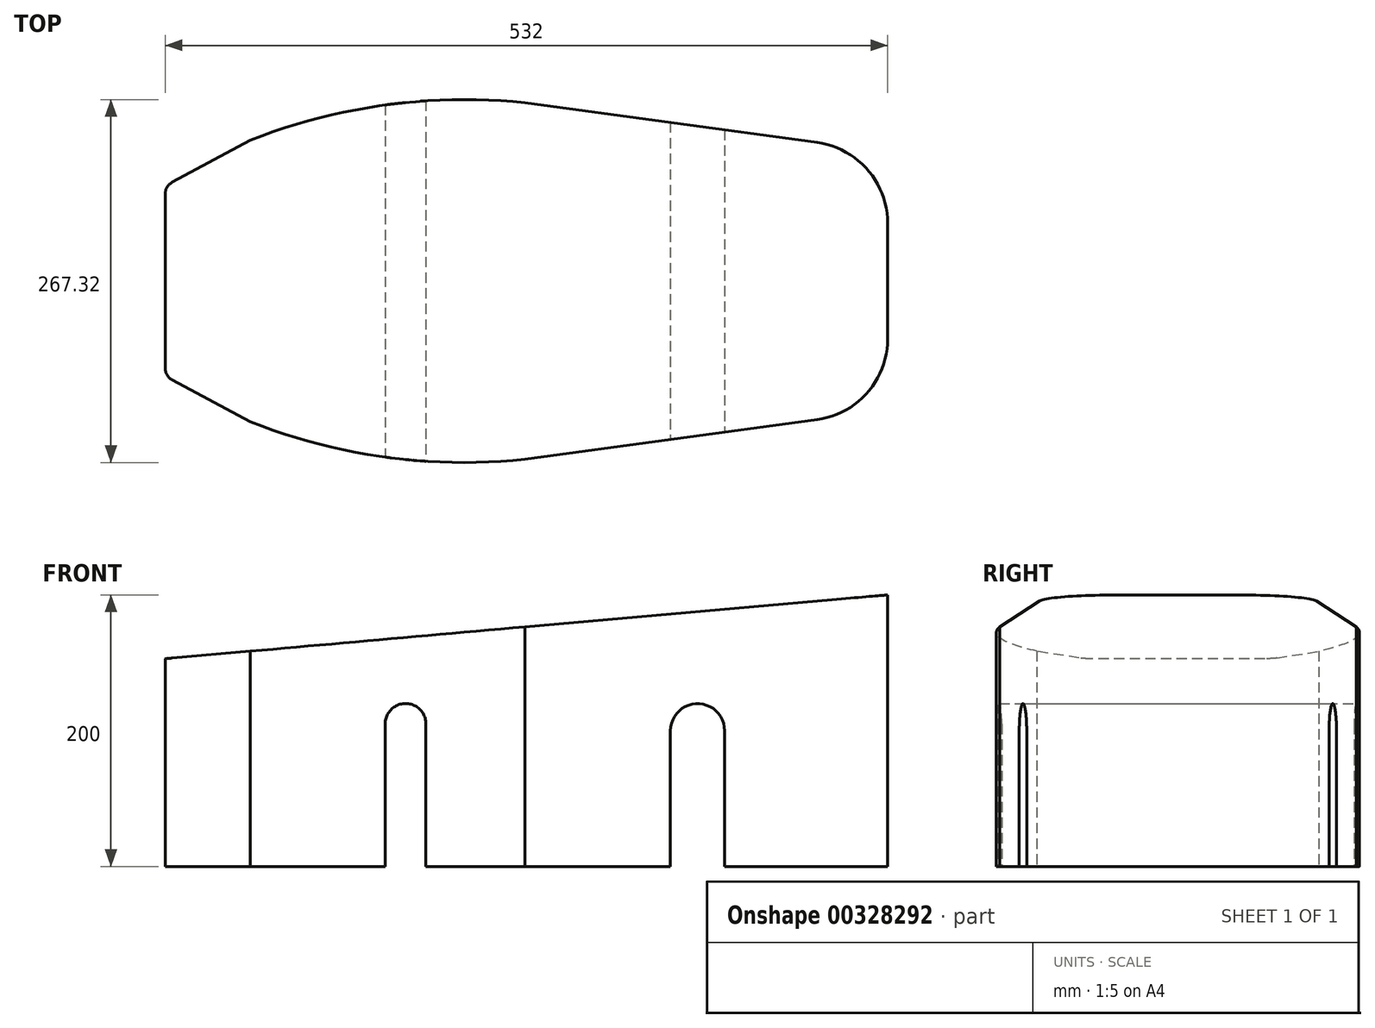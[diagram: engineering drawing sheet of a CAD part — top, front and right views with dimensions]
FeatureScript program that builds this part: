
annotation { "Feature Type Name" : "Feature", "Feature Type Description" : "" }
export const myFeature = defineFeature(function(context is Context, id is Id, definition is map)
    precondition{}
    {
        {
            var Q0;
            Q0=qCreatedBy(makeId("Top.planeOp"),FACE);
            var sketch = newSketch(context, id + "F0", { "sketchPlane" : qUnion([Q0])});
            skArc(sketch, "E0", {"start": v(-260.74, 72.83) * mm, "mid": v(-264.59, 69.15) * mm, "end": v(-266, 64.03) * mm});
            skLineSegment(sketch, "E1", {"start": v(-260.74, 72.83) * mm, "end": v(-203.32, 103.75) * mm});
            skArc(sketch, "E2", {"start": v(266, 42.61) * mm, "mid": v(251.2, 82.07) * mm, "end": v(214.1, 102.06) * mm});
            skLineSegment(sketch, "E3", {"start": v(-266, -64.03) * mm, "end": v(-266, 64.03) * mm});
            skLineSegment(sketch, "E4", {"start": v(-260.74, -72.83) * mm, "end": v(-203.32, -103.75) * mm});
            skArc(sketch, "E5", {"start": v(-266, -64.03) * mm, "mid": v(-264.59, -69.15) * mm, "end": v(-260.74, -72.83) * mm});
            skLineSegment(sketch, "E6", {"start": v(266, -42.61) * mm, "end": v(266, 42.61) * mm});
            skLineSegment(sketch, "E7", {"start": v(214.1, 102.06) * mm, "end": v(-1.08, 131.35) * mm});
            skArc(sketch, "E8", {"start": v(-1.08, 131.35) * mm, "mid": v(-103.86, 129.7) * mm, "end": v(-203.32, 103.75) * mm});
            skArc(sketch, "E9", {"start": v(214.1, -102.06) * mm, "mid": v(251.2, -82.07) * mm, "end": v(266, -42.61) * mm});
            skLineSegment(sketch, "E10", {"start": v(214.1, -102.06) * mm, "end": v(-1.08, -131.35) * mm});
            skArc(sketch, "E11", {"start": v(-203.32, -103.75) * mm, "mid": v(-103.86, -129.7) * mm, "end": v(-1.08, -131.35) * mm});
            skSolve(sketch);
        }
        {
            var Q0;
            Q0=makeQuery(id+"F0.imprint","IMPRINT",FACE,{"disambiguationData":[TD([[makeQuery(id+"F0.imprint","IMPRINT",EDGE,{"derivedFrom":sQuery(id+"F0.wireOp",EDGE,"E0")}),1.0]])]});
            extrude(context, id + "F1", {"entities" : qUnion([Q0]), "depth" : 200 * mm});
        }
        {
            var Q0;
            Q0=qCreatedBy(makeId("Front.planeOp"),FACE);
            var sketch = newSketch(context, id + "F2", { "sketchPlane" : qUnion([Q0])});
            skLineSegment(sketch, "E12.0", {"start": v(-266, 200) * mm, "end": v(-266, 153) * mm});
            skLineSegment(sketch, "E13.0", {"start": v(-266, 200) * mm, "end": v(266, 200) * mm});
            skLineSegment(sketch, "E14", {"start": v(266, 200) * mm, "end": v(-266, 153) * mm});
            skPoint(sketch, "E15.orphan", {"position": v(-203.32, 200) * mm});
            skPoint(sketch, "E16.orphan", {"position": v(-1.08, 200) * mm});
            skPoint(sketch, "E17.orphan", {"position": v(-266, 0) * mm});
            skPoint(sketch, "E18.0.end.orphan", {"position": v(266, 0) * mm});
            skSolve(sketch);
        }
        {
            var Q0;
            Q0 = qSketchRegion(id + "F2", true);
            extrude(context, id + "F3", {"entities" : qUnion([Q0]), "operationType" : NewBodyOperationType.REMOVE, "endBound" : BoundingType.SYMMETRIC, "oppositeDirection" : true, "depth" : 300 * mm});
        }
        {
            var Q0;
            Q0=qCreatedBy(makeId("Front.planeOp"),FACE);
            var sketch = newSketch(context, id + "F4", { "sketchPlane" : qUnion([Q0])});
            skLineSegment(sketch, "E19.bottom", {"start": v(106, 120) * mm, "end": v(146, 120) * mm});
            skLineSegment(sketch, "E19.top", {"start": v(106, 0) * mm, "end": v(146, 0) * mm});
            skLineSegment(sketch, "E19.left", {"start": v(106, 120) * mm, "end": v(106, 0) * mm});
            skLineSegment(sketch, "E19.right", {"start": v(146, 120) * mm, "end": v(146, 0) * mm});
            skLineSegment(sketch, "E20.bottom", {"start": v(-104, 120) * mm, "end": v(-74, 120) * mm});
            skLineSegment(sketch, "E20.top", {"start": v(-104, 0) * mm, "end": v(-74, 0) * mm});
            skLineSegment(sketch, "E20.left", {"start": v(-104, 120) * mm, "end": v(-104, 0) * mm});
            skLineSegment(sketch, "E20.right", {"start": v(-74, 120) * mm, "end": v(-74, 0) * mm});
            skSolve(sketch);
        }
        {
            var Q0;
            Q0 = qSketchRegion(id + "F4", true);
            extrude(context, id + "F5", {"entities" : qUnion([Q0]), "operationType" : NewBodyOperationType.REMOVE, "endBound" : BoundingType.SYMMETRIC, "oppositeDirection" : true, "depth" : 300 * mm});
        }
        {
            var Q0;
            Q0=makeQuery(id+"F5.boolean.opBoolean","COPY",EDGE,{"derivedFrom":makeQuery(id+"F5.opExtrude","SWEPT_EDGE",EDGE,{"disambiguationData":[OSD([sQuery(id+"F4.wireOp",EDGE,"E19.bottom"),sQuery(id+"F4.wireOp",EDGE,"E19.right")])]})});
            var Q1;
            Q1=makeQuery(id+"F5.boolean.opBoolean","COPY",EDGE,{"derivedFrom":makeQuery(id+"F5.opExtrude","SWEPT_EDGE",EDGE,{"disambiguationData":[OSD([sQuery(id+"F4.wireOp",EDGE,"E19.bottom"),sQuery(id+"F4.wireOp",EDGE,"E19.left")])]})});
            fillet(context, id + "F6", {"entities" : qUnion([Q0, Q1]), "radius" : 20 * mm, "tangentPropagation" : true, "allowEdgeOverflow" : false});
        }
        {
            var Q0;
            Q0=makeQuery(id+"F5.boolean.opBoolean","COPY",EDGE,{"derivedFrom":makeQuery(id+"F5.opExtrude","SWEPT_EDGE",EDGE,{"disambiguationData":[OSD([sQuery(id+"F4.wireOp",EDGE,"E20.bottom"),sQuery(id+"F4.wireOp",EDGE,"E20.right")])]})});
            var Q1;
            Q1=makeQuery(id+"F5.boolean.opBoolean","COPY",EDGE,{"derivedFrom":makeQuery(id+"F5.opExtrude","SWEPT_EDGE",EDGE,{"disambiguationData":[OSD([sQuery(id+"F4.wireOp",EDGE,"E20.bottom"),sQuery(id+"F4.wireOp",EDGE,"E20.left")])]})});
            fillet(context, id + "F7", {"entities" : qUnion([Q0, Q1]), "radius" : 15 * mm, "tangentPropagation" : true, "allowEdgeOverflow" : false});
        }
    });
